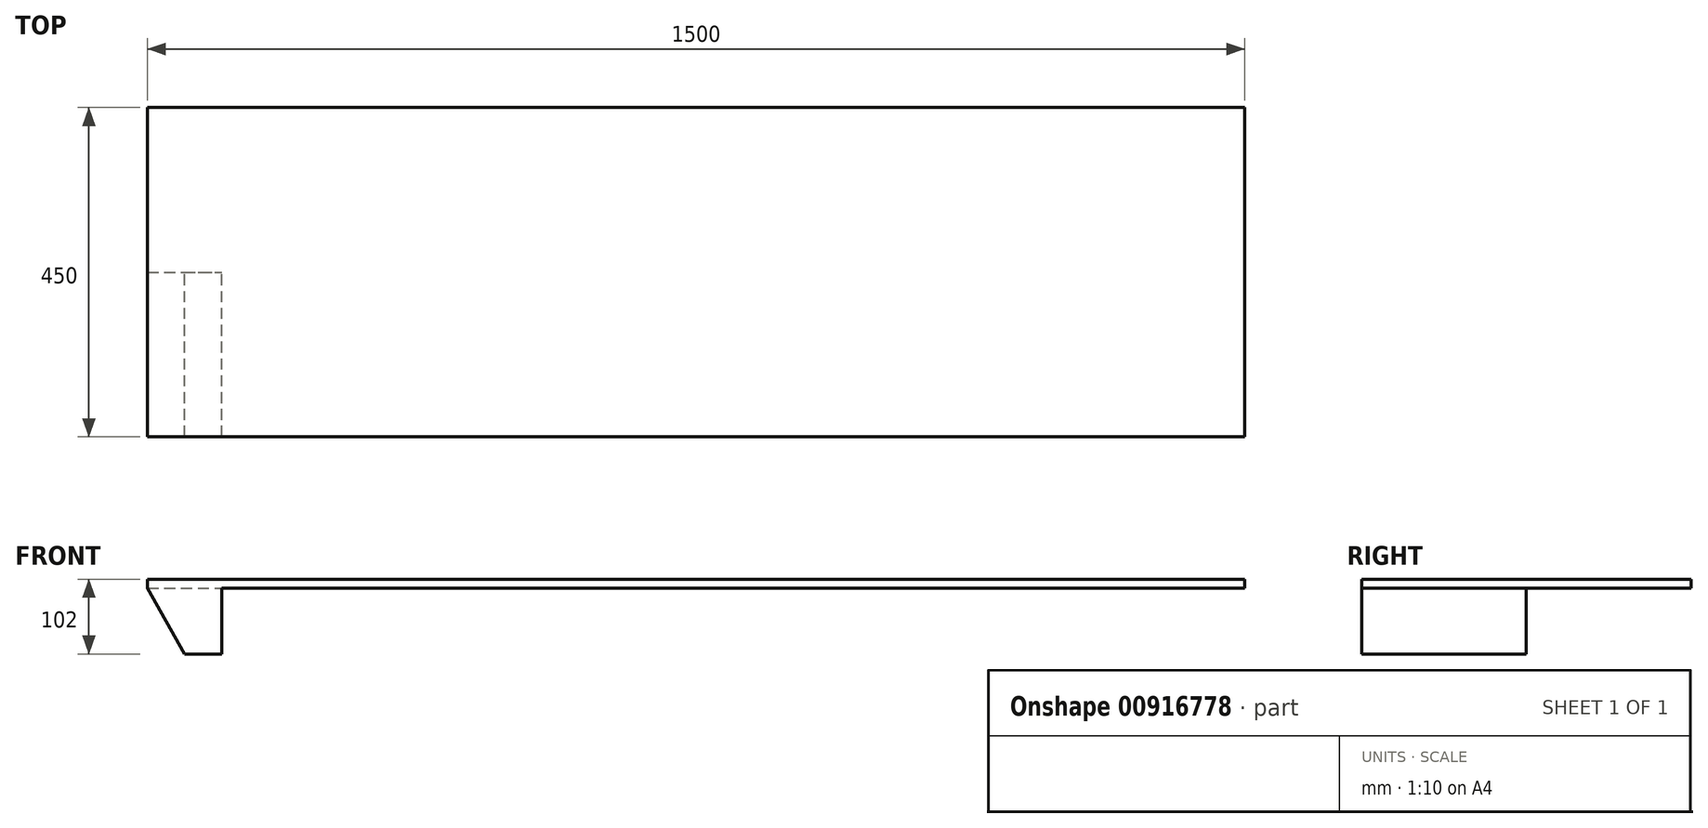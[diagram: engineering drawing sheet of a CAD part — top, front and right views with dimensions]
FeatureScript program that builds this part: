
annotation { "Feature Type Name" : "Feature", "Feature Type Description" : "" }
export const myFeature = defineFeature(function(context is Context, id is Id, definition is map)
    precondition{}
    {
        {
            var Q0;
            Q0=qCreatedBy(makeId("Front.planeOp"),FACE);
            var sketch = newSketch(context, id + "F0", { "sketchPlane" : qUnion([Q0])});
            skLineSegment(sketch, "E0.bottom", {"start": v(-750, 350) * mm, "end": v(750, 350) * mm});
            skLineSegment(sketch, "E0.top", {"start": v(-750, 0) * mm, "end": v(750, 0) * mm});
            skLineSegment(sketch, "E0.left", {"start": v(-750, 350) * mm, "end": v(-750, 0) * mm});
            skLineSegment(sketch, "E0.right", {"start": v(750, 350) * mm, "end": v(750, 0) * mm});
            skLineSegment(sketch, "E1", {"start": v(-750, 350) * mm, "end": v(-750, 338) * mm});
            skLineSegment(sketch, "E2", {"start": v(-750, 338) * mm, "end": v(-699.44, 248) * mm});
            skLineSegment(sketch, "E3", {"start": v(-699.44, 248) * mm, "end": v(-648.12, 248) * mm});
            skLineSegment(sketch, "E4", {"start": v(-648.12, 248) * mm, "end": v(-648.12, 282.9) * mm});
            skLineSegment(sketch, "E5", {"start": v(-648.12, 282.9) * mm, "end": v(0, 282.9) * mm});
            skLineSegment(sketch, "E6", {"start": v(0, 0) * mm, "end": v(0, 527.6) * mm, "construction": true});
            skSolve(sketch);
        }
        {
            var Q0;
            Q0=qCreatedBy(makeId("Front.planeOp"),FACE);
            var sketch = newSketch(context, id + "F1", { "sketchPlane" : qUnion([Q0])});
            skLineSegment(sketch, "E7.bottom", {"start": v(-750, 350) * mm, "end": v(750, 350) * mm});
            skLineSegment(sketch, "E7.top", {"start": v(-750, 338) * mm, "end": v(750, 338) * mm});
            skLineSegment(sketch, "E7.left", {"start": v(-750, 350) * mm, "end": v(-750, 338) * mm});
            skLineSegment(sketch, "E7.right", {"start": v(750, 350) * mm, "end": v(750, 338) * mm});
            skLineSegment(sketch, "E8.0", {"start": v(-750, 350) * mm, "end": v(-750, 338) * mm, "construction": true});
            skLineSegment(sketch, "E9.0", {"start": v(750, 350) * mm, "end": v(750, 0) * mm, "construction": true});
            skSolve(sketch);
        }
        {
            var Q0;
            Q0 = qSketchRegion(id + "F1", true);
            extrude(context, id + "F2", {"entities" : qUnion([Q0]), "endBound" : BoundingType.SYMMETRIC, "depth" : 450 * mm, "offsetDistance" : 25 * mm});
        }
        {
            var Q0;
            Q0=makeQuery(id+"F0.imprint","IMPRINT",FACE,{"disambiguationData":[TD([[makeQuery(id+"F0.imprint","IMPRINT",EDGE,{"derivedFrom":sQuery(id+"F0.wireOp",EDGE,"E0.bottom")}),-1.0]])]});
            var sketch = newSketch(context, id + "F3", { "sketchPlane" : qUnion([Q0])});
            skLineSegment(sketch, "E10.0", {"start": v(-750, 338) * mm, "end": v(-699.44, 248) * mm});
            skLineSegment(sketch, "E10.1", {"start": v(-699.44, 248) * mm, "end": v(-648.12, 248) * mm});
            skPoint(sketch, "E10.2", {"position": v(-648.12, 248) * mm});
            skLineSegment(sketch, "E10.3", {"start": v(-648.12, 248) * mm, "end": v(-648.12, 282.9) * mm});
            skPoint(sketch, "E10.4", {"position": v(-648.12, 265.45) * mm});
            skLineSegment(sketch, "E11", {"start": v(-750, 338) * mm, "end": v(-648.12, 338) * mm});
            skLineSegment(sketch, "E12", {"start": v(-648.12, 338) * mm, "end": v(-648.12, 282.9) * mm});
            skSolve(sketch);
        }
        {
            var Q0;
            Q0 = qSketchRegion(id + "F3", true);
            var Q1;
            Q1=makeQuery(id+"F2.opExtrude","CAP_VERTEX",VERTEX,{"disambiguationData":[OSD([sQuery(id+"F1.wireOp",EDGE,"E7.bottom"),sQuery(id+"F1.wireOp",EDGE,"E7.left")])],"isStart":false});
            extrude(context, id + "F4", {"entities" : qUnion([Q0]), "operationType" : NewBodyOperationType.ADD, "endBound" : BoundingType.UP_TO_VERTEX, "depth" : 25 * mm, "endBoundEntityVertex" : qUnion([Q1]), "offsetDistance" : 25 * mm});
        }
    });
